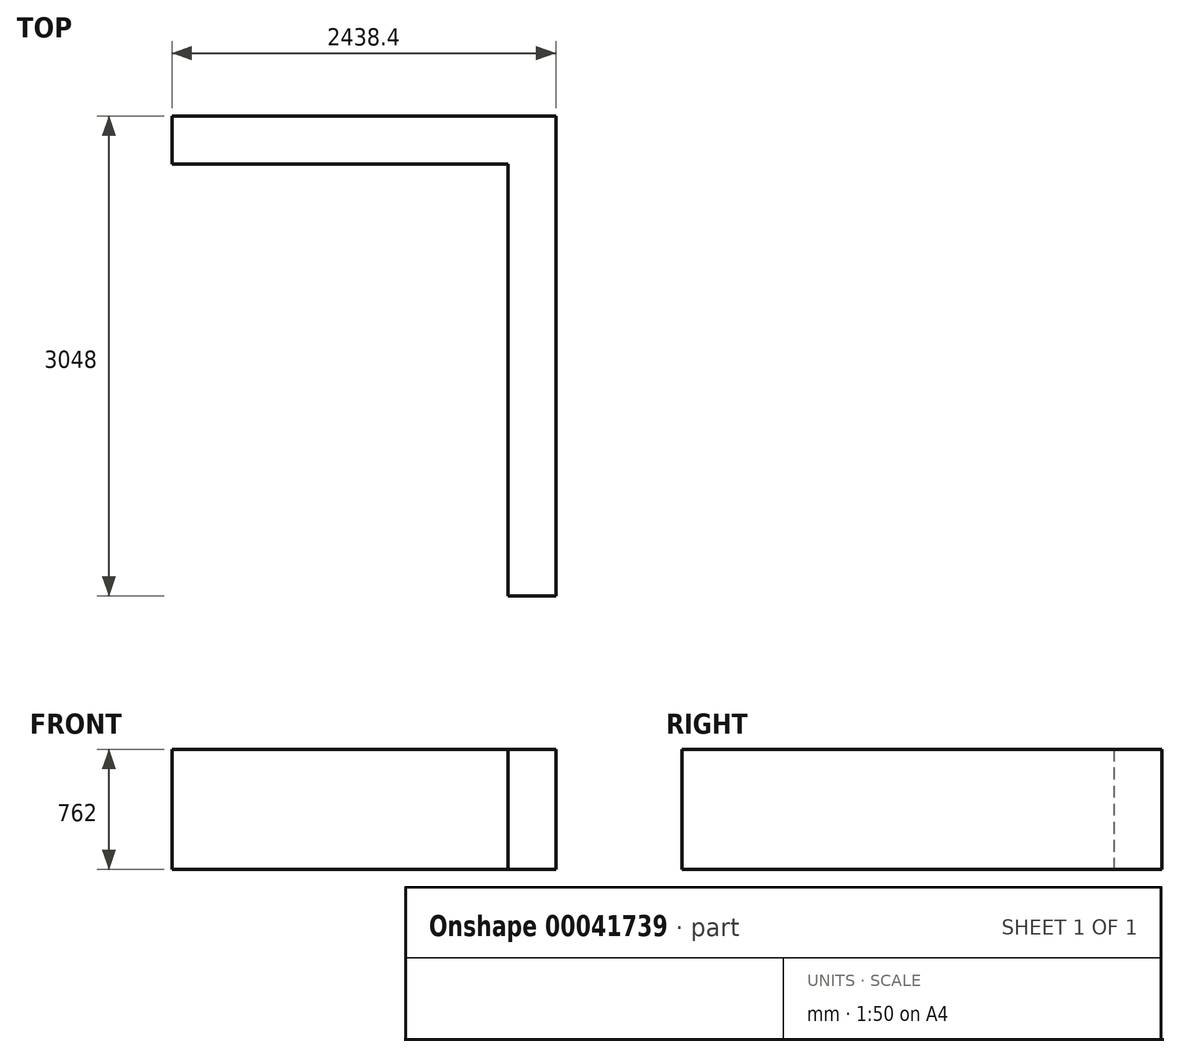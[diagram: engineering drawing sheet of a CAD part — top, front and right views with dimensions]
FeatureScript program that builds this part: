
annotation { "Feature Type Name" : "Feature", "Feature Type Description" : "" }
export const myFeature = defineFeature(function(context is Context, id is Id, definition is map)
    precondition{}
    {
        {
            var Q0;
            Q0=qCreatedBy(makeId("Top.planeOp"),FACE);
            var sketch = newSketch(context, id + "F0", { "sketchPlane" : qUnion([Q0])});
            skLineSegment(sketch, "E0.bottom", {"start": v(0, 0) * mm, "end": v(-2438.4, 0) * mm});
            skLineSegment(sketch, "E0.top", {"start": v(0, -304.8) * mm, "end": v(-2438.4, -304.8) * mm});
            skLineSegment(sketch, "E0.left", {"start": v(0, 0) * mm, "end": v(0, -304.8) * mm});
            skLineSegment(sketch, "E0.right", {"start": v(-2438.4, 0) * mm, "end": v(-2438.4, -304.8) * mm});
            skLineSegment(sketch, "E1.bottom", {"start": v(0, -304.8) * mm, "end": v(-304.8, -304.8) * mm});
            skLineSegment(sketch, "E1.top", {"start": v(0, -3048) * mm, "end": v(-304.8, -3048) * mm});
            skLineSegment(sketch, "E1.left", {"start": v(0, -304.8) * mm, "end": v(0, -3048) * mm});
            skLineSegment(sketch, "E1.right", {"start": v(-304.8, -304.8) * mm, "end": v(-304.8, -3048) * mm});
            skSolve(sketch);
        }
        {
            var Q0;
            Q0 = qSketchRegion(id + "F0", true);
            extrude(context, id + "F1", {"entities" : qUnion([Q0]), "depth" : 762 * mm, "offsetDistance" : 30.48 * mm});
        }
    });
